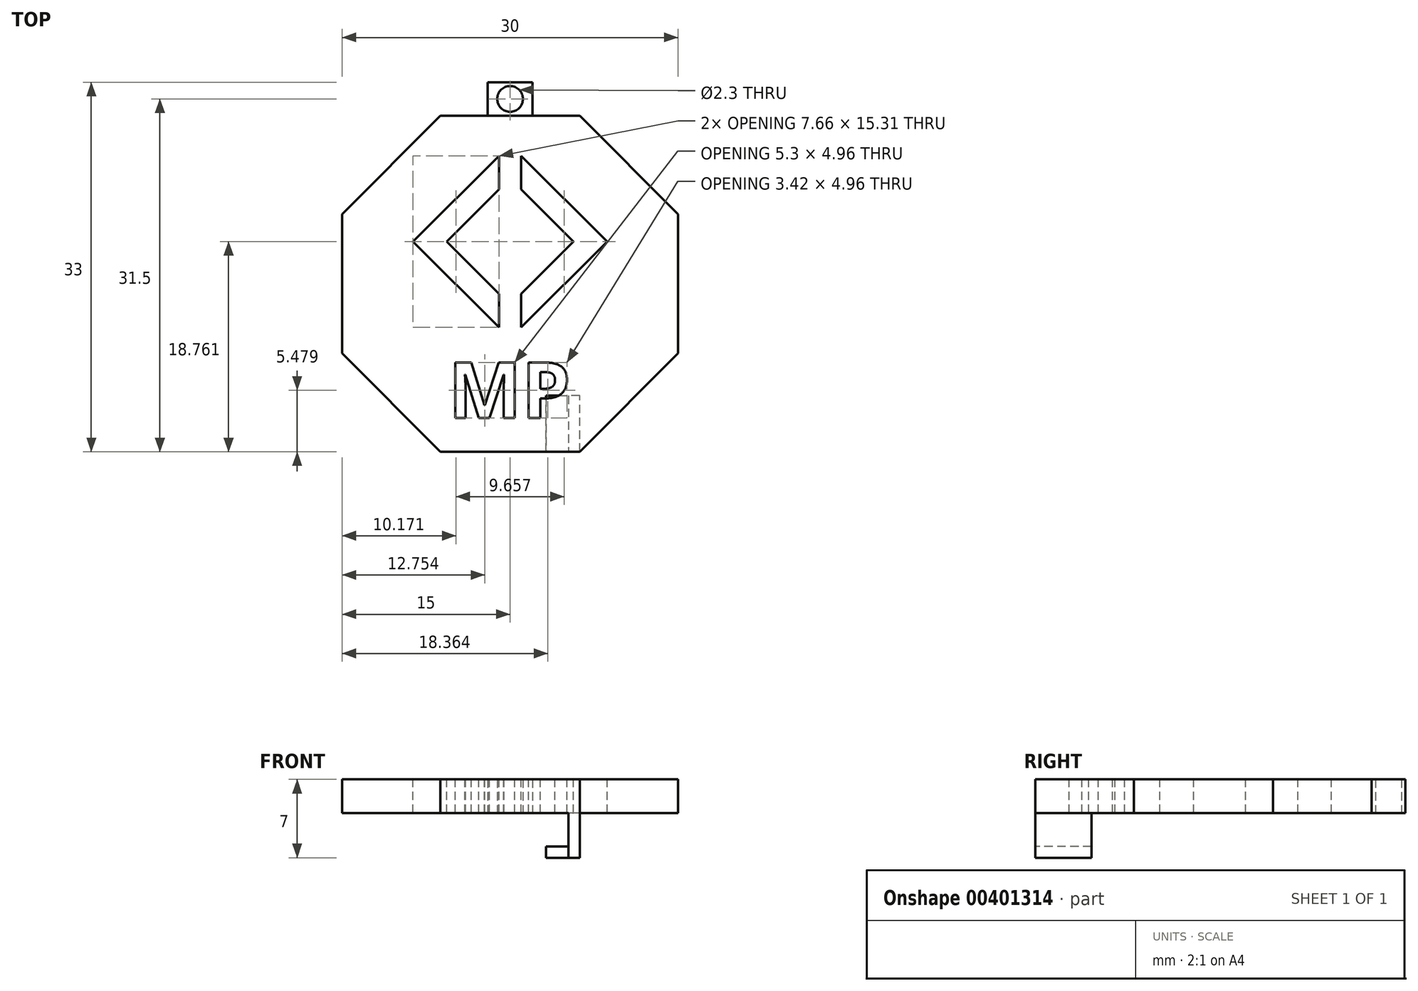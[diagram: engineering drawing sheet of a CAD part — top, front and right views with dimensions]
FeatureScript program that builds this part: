
annotation { "Feature Type Name" : "Feature", "Feature Type Description" : "" }
export const myFeature = defineFeature(function(context is Context, id is Id, definition is map)
    precondition{}
    {
        {
            var Q0;
            Q0=qCreatedBy(makeId("Top.planeOp"),FACE);
            var sketch = newSketch(context, id + "F0", { "sketchPlane" : qUnion([Q0])});
            skCircle(sketch, "E0.cCircle", {"center": v(0, 0) * mm, "radius": 15 * mm, "construction": true});
            skLineSegment(sketch, "E0.0", {"start": v(15, 6.21) * mm, "end": v(15, -6.21) * mm});
            skLineSegment(sketch, "E0.1", {"start": v(15, -6.21) * mm, "end": v(6.21, -15) * mm});
            skLineSegment(sketch, "E0.2", {"start": v(6.21, -15) * mm, "end": v(-6.21, -15) * mm});
            skLineSegment(sketch, "E0.3", {"start": v(-6.21, -15) * mm, "end": v(-15, -6.21) * mm});
            skLineSegment(sketch, "E0.4", {"start": v(-15, -6.21) * mm, "end": v(-15, 6.21) * mm});
            skLineSegment(sketch, "E0.5", {"start": v(-15, 6.21) * mm, "end": v(-6.21, 15) * mm});
            skLineSegment(sketch, "E0.6", {"start": v(-6.21, 15) * mm, "end": v(6.21, 15) * mm});
            skLineSegment(sketch, "E0.7", {"start": v(6.21, 15) * mm, "end": v(15, 6.21) * mm});
            skPoint(sketch, "E0.0.midPoint", {"position": v(15, 0) * mm});
            skLineSegment(sketch, "E1", {"start": v(0, 0) * mm, "end": v(-15, 0) * mm, "construction": true});
            skSolve(sketch);
        }
        {
            var Q0;
            Q0 = qSketchRegion(id + "F0", true);
            extrude(context, id + "F1", {"entities" : qUnion([Q0]), "depth" : 3 * mm});
        }
        {
            var Q0;
            Q0=makeQuery(id+"F1.opExtrude","CAP_FACE",FACE,{"disambiguationData":[OSD([sQuery(id+"F0.wireOp",EDGE,"E0.0"),sQuery(id+"F0.wireOp",EDGE,"E0.1"),sQuery(id+"F0.wireOp",EDGE,"E0.2"),sQuery(id+"F0.wireOp",EDGE,"E0.3"),sQuery(id+"F0.wireOp",EDGE,"E0.4"),sQuery(id+"F0.wireOp",EDGE,"E0.5"),sQuery(id+"F0.wireOp",EDGE,"E0.6"),sQuery(id+"F0.wireOp",EDGE,"E0.7")])],"isStart":false});
            var sketch = newSketch(context, id + "F2", { "sketchPlane" : qUnion([Q0])});
            skText(sketch, "E2", { "text": "MP", "fontName": "OpenSans-Bold.ttf"});
            skArc(sketch, "E3.cCircle", {"start": v(2.83, 0.93) * mm, "mid": v(0, 7.76) * mm, "end": v(-2.83, 0.93) * mm, "construction": true});
            skLineSegment(sketch, "E3.0", {"start": v(5.66, 3.76) * mm, "end": v(1, -0.9) * mm});
            skLineSegment(sketch, "E3.2", {"start": v(-5.66, 3.76) * mm, "end": v(-1, 8.42) * mm});
            skLineSegment(sketch, "E3.3", {"start": v(1, 8.42) * mm, "end": v(5.66, 3.76) * mm});
            skPoint(sketch, "E3.0.midPoint", {"position": v(2.83, 0.93) * mm});
            skLineSegment(sketch, "E4", {"start": v(-5.66, 3.76) * mm, "end": v(0, 3.76) * mm, "construction": true});
            skLineSegment(sketch, "E5.1", {"start": v(8.66, 3.76) * mm, "end": v(1, -3.9) * mm});
            skLineSegment(sketch, "E5.3", {"start": v(-8.66, 3.76) * mm, "end": v(-1, 11.42) * mm});
            skPoint(sketch, "E5.0.midPoint", {"position": v(4.33, 8.1) * mm});
            skLineSegment(sketch, "E6", {"start": v(-8.66, 3.76) * mm, "end": v(-5.66, 3.76) * mm, "construction": true});
            skPoint(sketch, "E7.orphan", {"position": v(0, -1.9) * mm});
            skPoint(sketch, "E8.orphan", {"position": v(0, -4.9) * mm});
            skPoint(sketch, "E9.orphan", {"position": v(0.45, -660.17) * mm});
            skPoint(sketch, "E10.orphan", {"position": v(-0.45, -23.95) * mm});
            skLineSegment(sketch, "E11.trimOffspring", {"start": v(0, 3.76) * mm, "end": v(8.66, 3.76) * mm, "construction": true});
            skPoint(sketch, "E12.orphan", {"position": v(0, 9.42) * mm});
            skPoint(sketch, "E13.orphan", {"position": v(0, 12.42) * mm});
            skPoint(sketch, "E14.bottom.end.orphan", {"position": v(0.45, 31.48) * mm});
            skPoint(sketch, "E14.bottom.start.orphan", {"position": v(-0.45, 667.69) * mm});
            skPoint(sketch, "E15.firstSnap0", {"position": v(-10.6, -10.6) * mm});
            skPoint(sketch, "E15.secondSnap0", {"position": v(10.6, 10.6) * mm});
            skPoint(sketch, "E16.startSnap0", {"position": v(0.45, 11.37) * mm});
            skLineSegment(sketch, "E17", {"start": v(1, 11.42) * mm, "end": v(1, 8.42) * mm});
            skLineSegment(sketch, "E18", {"start": v(-1, 11.42) * mm, "end": v(-1, 8.42) * mm});
            skPoint(sketch, "E19.orphan", {"position": v(0.45, 12.87) * mm});
            skLineSegment(sketch, "E20.trimOffspring", {"start": v(1, 11.42) * mm, "end": v(8.66, 3.76) * mm});
            skPoint(sketch, "E21.trimOffspring.end.orphan", {"position": v(0.45, 9.87) * mm});
            skLineSegment(sketch, "E22.trimOffspring", {"start": v(-1, -0.9) * mm, "end": v(-5.66, 3.76) * mm});
            skLineSegment(sketch, "E23.trimOffspring", {"start": v(-1, -0.9) * mm, "end": v(-1, -3.9) * mm});
            skLineSegment(sketch, "E24.trimOffspring", {"start": v(1, -0.9) * mm, "end": v(1, -3.9) * mm});
            skLineSegment(sketch, "E25.trimOffspring", {"start": v(-1, -3.9) * mm, "end": v(-8.66, 3.76) * mm});
            const initialGuessF2  = {"E2": [-0.00552, -0.012, 1, 0, 0.005]};
            skSetInitialGuess(sketch, initialGuessF2);
            skSolve(sketch);
        }
        {
            var Q0;
            Q0 = qSketchRegion(id + "F2", true);
            extrude(context, id + "F3", {"entities" : qUnion([Q0]), "operationType" : NewBodyOperationType.REMOVE, "endBound" : BoundingType.THROUGH_ALL, "oppositeDirection" : true, "depth" : 3 * mm});
        }
        {
            var Q0;
            Q0=makeQuery(id+"F1.opExtrude","CAP_FACE",FACE,{"disambiguationData":[OSD([sQuery(id+"F0.wireOp",EDGE,"E0.0"),sQuery(id+"F0.wireOp",EDGE,"E0.1"),sQuery(id+"F0.wireOp",EDGE,"E0.2"),sQuery(id+"F0.wireOp",EDGE,"E0.3"),sQuery(id+"F0.wireOp",EDGE,"E0.4"),sQuery(id+"F0.wireOp",EDGE,"E0.5"),sQuery(id+"F0.wireOp",EDGE,"E0.6"),sQuery(id+"F0.wireOp",EDGE,"E0.7")])],"isStart":true});
            var sketch = newSketch(context, id + "F4", { "sketchPlane" : qUnion([Q0])});
            skLineSegment(sketch, "E26.bottom", {"start": v(6.21, 15) * mm, "end": v(5.21, 15) * mm});
            skLineSegment(sketch, "E26.top", {"start": v(6.21, 10) * mm, "end": v(5.21, 10) * mm});
            skLineSegment(sketch, "E26.left", {"start": v(6.21, 15) * mm, "end": v(6.21, 10) * mm});
            skLineSegment(sketch, "E26.right", {"start": v(5.21, 15) * mm, "end": v(5.21, 10) * mm});
            skSolve(sketch);
        }
        {
            var Q0;
            Q0 = qSketchRegion(id + "F4", true);
            extrude(context, id + "F5", {"entities" : qUnion([Q0]), "operationType" : NewBodyOperationType.ADD, "depth" : 4 * mm});
        }
        {
            var Q0;
            Q0=makeQuery(id+"F5.opExtrude","SWEPT_FACE",FACE,{"disambiguationData":[OSD([sQuery(id+"F4.wireOp",EDGE,"E26.right")])]});
            var sketch = newSketch(context, id + "F6", { "sketchPlane" : qUnion([Q0])});
            skLineSegment(sketch, "E27.bottom", {"start": v(10, -4) * mm, "end": v(15, -4) * mm});
            skLineSegment(sketch, "E27.top", {"start": v(10, -3) * mm, "end": v(15, -3) * mm});
            skLineSegment(sketch, "E27.left", {"start": v(10, -4) * mm, "end": v(10, -3) * mm});
            skLineSegment(sketch, "E27.right", {"start": v(15, -4) * mm, "end": v(15, -3) * mm});
            skSolve(sketch);
        }
        {
            var Q0;
            Q0=makeQuery(id+"F6.imprint","IMPRINT",FACE,{"disambiguationData":[TD([[makeQuery(id+"F6.imprint","IMPRINT",EDGE,{"derivedFrom":sQuery(id+"F6.wireOp",EDGE,"E27.bottom")}),-1.0]])]});
            var Q1;
            Q1=sQuery(id+"F6.wireOp",EDGE,"E27.top");
            var Q2;
            Q2=sQuery(id+"F6.wireOp",EDGE,"E27.bottom");
            var Q3;
            Q3=sQuery(id+"F6.wireOp",EDGE,"E27.right");
            var Q4;
            Q4=sQuery(id+"F6.wireOp",EDGE,"E27.left");
            extrude(context, id + "F7", {"entities" : qUnion([Q0]), "surfaceEntities" : qUnion([Q1, Q2, Q3, Q4]), "depth" : 2 * mm});
        }
        {
            var Q0;
            Q0=makeQuery(id+"F1.opExtrude","SWEPT_FACE",FACE,{"disambiguationData":[OSD([sQuery(id+"F0.wireOp",EDGE,"E0.6")])]});
            var sketch = newSketch(context, id + "F8", { "sketchPlane" : qUnion([Q0])});
            skLineSegment(sketch, "E28.bottom", {"start": v(2, 3) * mm, "end": v(-2, 3) * mm});
            skLineSegment(sketch, "E28.top", {"start": v(2, 0) * mm, "end": v(-2, 0) * mm});
            skLineSegment(sketch, "E28.left", {"start": v(2, 3) * mm, "end": v(2, 0) * mm});
            skLineSegment(sketch, "E28.right", {"start": v(-2, 3) * mm, "end": v(-2, 0) * mm});
            skPoint(sketch, "E28.middle", {"position": v(0, 1.5) * mm});
            skPoint(sketch, "E28.middle.positionSnap0", {"position": v(0, 3) * mm});
            skPoint(sketch, "E28.centerSnap0", {"position": v(0, 3) * mm});
            skSolve(sketch);
        }
        {
            var Q0;
            Q0 = qSketchRegion(id + "F8", true);
            extrude(context, id + "F9", {"entities" : qUnion([Q0]), "depth" : 3 * mm});
        }
        {
            var Q0;
            Q0=makeQuery(id+"F9.opExtrude","SWEPT_FACE",FACE,{"disambiguationData":[OSD([sQuery(id+"F8.wireOp",EDGE,"E28.top")])]});
            var sketch = newSketch(context, id + "F10", { "sketchPlane" : qUnion([Q0])});
            skCircle(sketch, "E29", {"center": v(0, -16.5) * mm, "radius": 1.15 * mm});
            skLineSegment(sketch, "E30", {"start": v(0, -16.5) * mm, "end": v(0, -15) * mm, "construction": true});
            skLineSegment(sketch, "E31", {"start": v(0, -16.5) * mm, "end": v(0, -18) * mm, "construction": true});
            skSolve(sketch);
        }
        {
            var Q0;
            Q0 = qSketchRegion(id + "F10", true);
            extrude(context, id + "F11", {"entities" : qUnion([Q0]), "operationType" : NewBodyOperationType.REMOVE, "endBound" : BoundingType.THROUGH_ALL, "oppositeDirection" : true, "depth" : 25 * mm});
        }
    });
